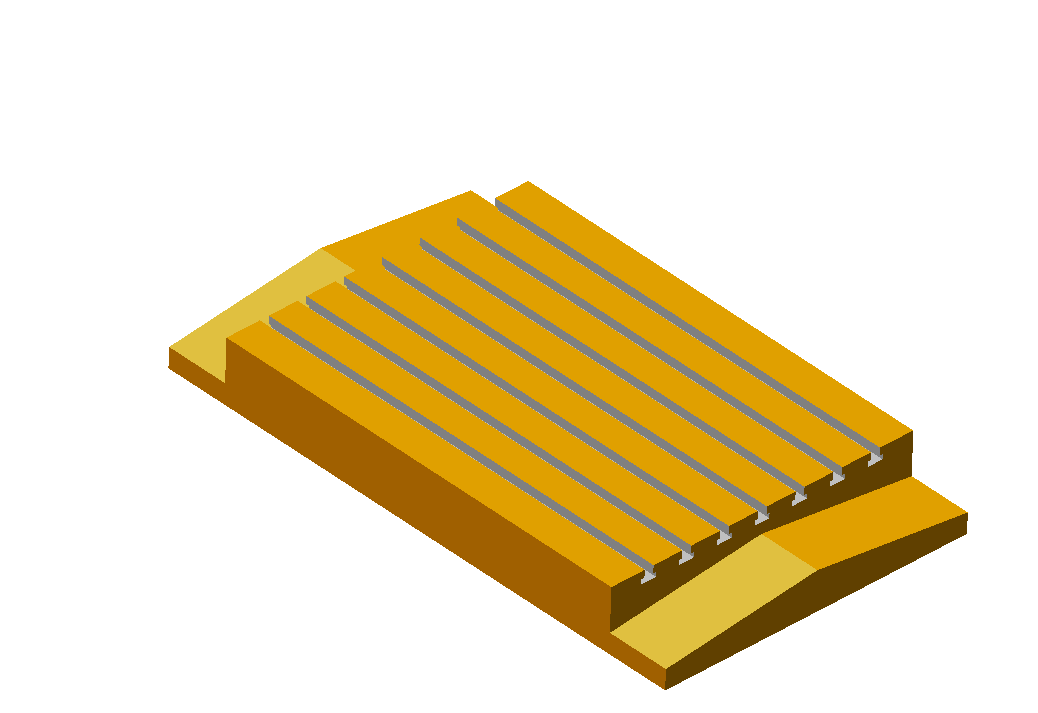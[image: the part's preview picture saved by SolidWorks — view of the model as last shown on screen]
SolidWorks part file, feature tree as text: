
SOLIDWORKS PART (.sldprt)
format: sldprt  version: not decoded by parser v0  size: 538,624 bytes
history: native  units: mm
features: thread x8, sketch x7, extrude x3, pattern_linear x2, shell x1, mirror x1, plane x1, fillet x1, cut_extrude x1, hole x1 (+10 scaffold rows collapsed)
feature tree (36):
  scaffold x10  (default folders/planes/origin — collapsed)
  pattern_linear  "LPattern1"  [2 undecoded]
  extrude  "Boss-Extrude2"  [1 undecoded]
  sketch  "Sketch3"
  extrude  "Base-Extrude"  [1 undecoded]
  sketch  "Sketch1"  dims[c1.D1=203.2mm c1.D2=1016.0mm c2.D1=1397.0mm]
  shell  "Shell1"  [1 undecoded]
  extrude  "Boss-Extrude1"  [1 undecoded]
  sketch  "Sketch2"  dims[c1.D1=127.0mm c1.D2=~512.23881mm c2.D2=7.0deg c2.D1=203.2mm]
  mirror  "Mirror1"
  plane  "Plane1"  Offset=50mm
  sketch  "Sketch4"  dims[c1.D1=600.0mm c1.D2=800.0mm c1.D3=400.0mm c2.D1=50.8mm]
  fillet  "Fillet1"  Radius=12.7mm
  sketch  "Sketch5"  dims[c1.D1=50.0mm c1.D2=16.0mm c1.D3=30.0mm c1.D4=30.0mm c1.D5=10.0mm c1.Cutter_width=50.0mm c1.Cutter_hieght=16.0mm c1.Arbor_width=30.0mm c2.D4=95.0mm c2.Depth=40.0mm c3.D4=111.76mm]
  cut_extrude  "TSLOT1"  [1 undecoded]
  pattern_linear  "LPattern2"  Count1=7 Count2=1 Spacing1=127mm Spacing2=546.1mm
  hole  "1-8 Tapped Hole1"  Diameter=22.225mm Depth=43.18mm
  sketch  "Sketch7"
  sketch  "Sketch6"  dims[hole-wizard template sketch: 46 standard entries collapsed; hole parameters kept: c15.Hole Dia.=22.225mm c15.Hole Depth=43.18mm c15.D3=~14.816244mm c15.Drill Angle=118.0deg]
  thread  "Cosmetic Thread1"  Diameter=43.18mm  [1 undecoded]
  thread  "Cosmetic Thread2"  Diameter=43.18mm  [1 undecoded]
  thread  "Cosmetic Thread3"  Diameter=43.18mm  [1 undecoded]
  thread  "Cosmetic Thread4"  Diameter=43.18mm  [1 undecoded]
  thread  "Cosmetic Thread5"  Diameter=43.18mm  [1 undecoded]
  thread  "Cosmetic Thread6"  Diameter=43.18mm  [1 undecoded]
  thread  "Cosmetic Thread7"  Diameter=43.18mm  [1 undecoded]
  thread  "Cosmetic Thread8"  Diameter=43.18mm  [1 undecoded]
decode coverage: 16 of 25 modeling features carry decoded parameters
note: ~ marks probable driven/reference dimensions
note: 15 parameter values undecoded
summary: no parameter record found for 5 features
note: suppression state not decoded; provenance and decode notes live in map.json
